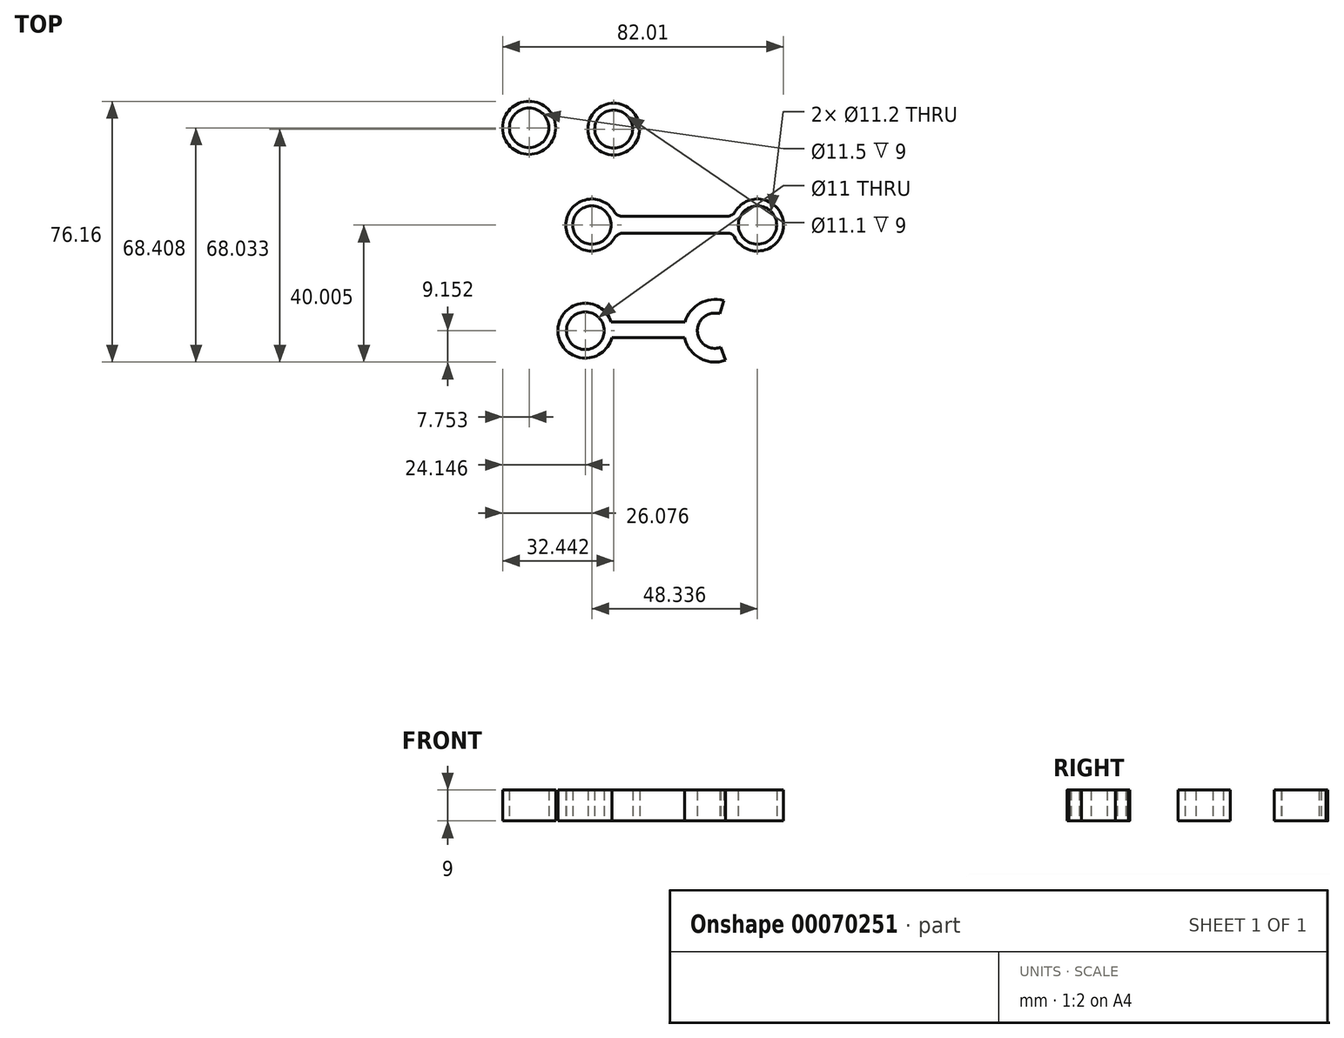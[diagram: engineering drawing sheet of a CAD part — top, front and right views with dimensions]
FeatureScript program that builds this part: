
annotation { "Feature Type Name" : "Feature", "Feature Type Description" : "" }
export const myFeature = defineFeature(function(context is Context, id is Id, definition is map)
    precondition{}
    {
        {
            var Q0;
            Q0=qCreatedBy(makeId("Top.planeOp"),FACE);
            var sketch = newSketch(context, id + "F0", { "sketchPlane" : qUnion([Q0])});
            skCircle(sketch, "E0", {"center": v(-32.87, 26.06) * mm, "radius": 5.6 * mm});
            skCircle(sketch, "E1", {"center": v(15.46, 26.06) * mm, "radius": 5.6 * mm});
            skCircle(sketch, "E2", {"center": v(-34.8, -4.8) * mm, "radius": 5.5 * mm});
            skCircle(sketch, "E3", {"center": v(3.08, -4.8) * mm, "radius": 5.15 * mm});
            skLineSegment(sketch, "E4", {"start": v(-32.87, 26.06) * mm, "end": v(15.46, 26.06) * mm});
            skLineSegment(sketch, "E5", {"start": v(3.08, -4.8) * mm, "end": v(-34.8, -4.8) * mm});
            skCircle(sketch, "E6", {"center": v(-32.87, 26.06) * mm, "radius": 7.6 * mm});
            skCircle(sketch, "E7", {"center": v(15.46, 26.06) * mm, "radius": 7.6 * mm});
            skCircle(sketch, "E8", {"center": v(-34.8, -4.8) * mm, "radius": 8 * mm});
            skCircle(sketch, "E9", {"center": v(3.08, -4.8) * mm, "radius": 9.15 * mm});
            skLineSegment(sketch, "E10", {"start": v(15.46, 26.06) * mm, "end": v(20.01, 32.14) * mm});
            skLineSegment(sketch, "E11", {"start": v(15.46, 26.06) * mm, "end": v(13.27, 18.78) * mm});
            skLineSegment(sketch, "E12", {"start": v(3.08, -4.8) * mm, "end": v(5.57, 4) * mm});
            skLineSegment(sketch, "E13", {"start": v(3.08, -4.8) * mm, "end": v(6.09, -13.44) * mm});
            skLineSegment(sketch, "E14", {"start": v(-25.72, 28.6) * mm, "end": v(8.3, 28.6) * mm});
            skLineSegment(sketch, "E15", {"start": v(-25.66, 23.67) * mm, "end": v(8.25, 23.67) * mm});
            skLineSegment(sketch, "E16", {"start": v(-27.22, -2.25) * mm, "end": v(-5.71, -2.25) * mm});
            skLineSegment(sketch, "E17", {"start": v(-27.08, -6.86) * mm, "end": v(-5.84, -6.86) * mm});
            skCircle(sketch, "E18", {"center": v(-23.97, 31.37) * mm, "radius": 2.77 * mm});
            skCircle(sketch, "E19", {"center": v(-23.82, 20.8) * mm, "radius": 2.87 * mm});
            skCircle(sketch, "E20", {"center": v(6.54, 31.42) * mm, "radius": 2.81 * mm});
            skCircle(sketch, "E21", {"center": v(7, 21.78) * mm, "radius": 1.89 * mm});
            skSolve(sketch);
        }
        {
            var Q0;
            Q0=makeQuery(id+"F0.imprint","IMPRINT",FACE,{"disambiguationData":[TD([[makeQuery(id+"F0.imprint","IMPRINT",EDGE,{"derivedFrom":sQuery(id+"F0.wireOp",EDGE,"E0")}),-1.0]])]});
            var Q1;
            {var subQ5=sQuery(id+"F0.wireOp",EDGE,"E15");Q1=makeQuery(id+"F0.imprint","IMPRINT",FACE,{"disambiguationData":[TD([[makeQuery(id+"F0.imprint","IMPRINT",EDGE,{"derivedFrom":subQ5}),1.0]])]});}
            var Q2;
            {var subQ5=sQuery(id+"F0.wireOp",EDGE,"E14");Q2=makeQuery(id+"F0.imprint","IMPRINT",FACE,{"disambiguationData":[TD([[makeQuery(id+"F0.imprint","IMPRINT",EDGE,{"derivedFrom":subQ5}),-1.0]])]});}
            var Q3;
            {var subQ4=sQuery(id+"F0.wireOp",EDGE,"E4");var subQ6=sQuery(id+"F0.wireOp",EDGE,"E1");var subQ7=makeQuery(id+"F0.imprint","INTERSECT",VERTEX,{"derivedFrom":[subQ6,subQ4]});Q3=makeQuery(id+"F0.imprint","IMPRINT",FACE,{"disambiguationData":[TD([[makeQuery(id+"F0.imprint","IMPRINT",EDGE,{"disambiguationData":[TD([[subQ7,-1.0]])],"derivedFrom":subQ6}),-1.0]])]});}
            var Q4;
            {var subQ0=sQuery(id+"F0.wireOp",EDGE,"E4");var subQ1=sQuery(id+"F0.wireOp",EDGE,"E1");var subQ2=makeQuery(id+"F0.imprint","INTERSECT",VERTEX,{"derivedFrom":[subQ1,subQ0]});Q4=makeQuery(id+"F0.imprint","IMPRINT",FACE,{"disambiguationData":[TD([[makeQuery(id+"F0.imprint","IMPRINT",EDGE,{"disambiguationData":[TD([[subQ2,1.0]])],"derivedFrom":subQ1}),-1.0]])]});}
            var Q5;
            Q5=makeQuery(id+"F0.imprint","IMPRINT",FACE,{"disambiguationData":[TD([[makeQuery(id+"F0.imprint","IMPRINT",EDGE,{"derivedFrom":sQuery(id+"F0.wireOp",EDGE,"E2")}),-1.0]])]});
            var Q6;
            {var subQ5=sQuery(id+"F0.wireOp",EDGE,"E16");Q6=makeQuery(id+"F0.imprint","IMPRINT",FACE,{"disambiguationData":[TD([[makeQuery(id+"F0.imprint","IMPRINT",EDGE,{"derivedFrom":subQ5}),-1.0]])]});}
            var Q7;
            {var subQ5=sQuery(id+"F0.wireOp",EDGE,"E17");Q7=makeQuery(id+"F0.imprint","IMPRINT",FACE,{"disambiguationData":[TD([[makeQuery(id+"F0.imprint","IMPRINT",EDGE,{"derivedFrom":subQ5}),1.0]])]});}
            var Q8;
            {var subQ4=sQuery(id+"F0.wireOp",EDGE,"E5");var subQ6=sQuery(id+"F0.wireOp",EDGE,"E3");var subQ7=makeQuery(id+"F0.imprint","INTERSECT",VERTEX,{"derivedFrom":[subQ6,subQ4]});Q8=makeQuery(id+"F0.imprint","IMPRINT",FACE,{"disambiguationData":[TD([[makeQuery(id+"F0.imprint","IMPRINT",EDGE,{"disambiguationData":[TD([[subQ7,-1.0]])],"derivedFrom":subQ6}),-1.0]])]});}
            var Q9;
            {var subQ2=sQuery(id+"F0.wireOp",EDGE,"E5");var subQ6=sQuery(id+"F0.wireOp",EDGE,"E3");var subQ7=makeQuery(id+"F0.imprint","INTERSECT",VERTEX,{"derivedFrom":[subQ6,subQ2]});Q9=makeQuery(id+"F0.imprint","IMPRINT",FACE,{"disambiguationData":[TD([[makeQuery(id+"F0.imprint","IMPRINT",EDGE,{"disambiguationData":[TD([[subQ7,1.0]])],"derivedFrom":subQ6}),-1.0]])]});}
            var Q10;
            {var subQ0=sQuery(id+"F0.wireOp",EDGE,"E10");var subQ1=sQuery(id+"F0.wireOp",EDGE,"E1");var subQ2=makeQuery(id+"F0.imprint","INTERSECT",VERTEX,{"derivedFrom":[subQ1,subQ0]});Q10=makeQuery(id+"F0.imprint","IMPRINT",FACE,{"disambiguationData":[TD([[makeQuery(id+"F0.imprint","IMPRINT",EDGE,{"disambiguationData":[TD([[subQ2,1.0]])],"derivedFrom":subQ1}),-1.0]])]});}
            var Q11;
            {var subQ0=sQuery(id+"F0.wireOp",EDGE,"E14");var subQ1=sQuery(id+"F0.wireOp",EDGE,"E6");var subQ2=makeQuery(id+"F0.imprint","INTERSECT",VERTEX,{"derivedFrom":[subQ1,subQ0]});Q11=makeQuery(id+"F0.imprint","IMPRINT",FACE,{"disambiguationData":[TD([[makeQuery(id+"F0.imprint","IMPRINT",EDGE,{"disambiguationData":[TD([[subQ2,-1.0]])],"derivedFrom":subQ1}),-1.0]])]});}
            var Q12;
            {var subQ0=sQuery(id+"F0.wireOp",EDGE,"E15");var subQ1=sQuery(id+"F0.wireOp",EDGE,"E6");var subQ2=makeQuery(id+"F0.imprint","INTERSECT",VERTEX,{"derivedFrom":[subQ1,subQ0]});Q12=makeQuery(id+"F0.imprint","IMPRINT",FACE,{"disambiguationData":[TD([[makeQuery(id+"F0.imprint","IMPRINT",EDGE,{"disambiguationData":[TD([[subQ2,1.0]])],"derivedFrom":subQ1}),-1.0]])]});}
            var Q13;
            {var subQ0=sQuery(id+"F0.wireOp",EDGE,"E14");var subQ1=sQuery(id+"F0.wireOp",EDGE,"E7");var subQ2=makeQuery(id+"F0.imprint","INTERSECT",VERTEX,{"derivedFrom":[subQ1,subQ0]});Q13=makeQuery(id+"F0.imprint","IMPRINT",FACE,{"disambiguationData":[TD([[makeQuery(id+"F0.imprint","IMPRINT",EDGE,{"disambiguationData":[TD([[subQ2,1.0]])],"derivedFrom":subQ1}),-1.0]])]});}
            var Q14;
            {var subQ0=sQuery(id+"F0.wireOp",EDGE,"E15");var subQ1=sQuery(id+"F0.wireOp",EDGE,"E7");var subQ2=makeQuery(id+"F0.imprint","INTERSECT",VERTEX,{"derivedFrom":[subQ1,subQ0]});Q14=makeQuery(id+"F0.imprint","IMPRINT",FACE,{"disambiguationData":[TD([[makeQuery(id+"F0.imprint","IMPRINT",EDGE,{"disambiguationData":[TD([[subQ2,-1.0]])],"derivedFrom":subQ1}),-1.0]])]});}
            extrude(context, id + "F1", {"entities" : qUnion([Q0, Q1, Q2, Q3, Q4, Q5, Q6, Q7, Q8, Q9, Q10, Q11, Q12, Q13, Q14]), "depth" : 9 * mm});
        }
        {
            var Q0;
            Q0=qCreatedBy(makeId("Top.planeOp"),FACE);
            var sketch = newSketch(context, id + "F2", { "sketchPlane" : qUnion([Q0])});
            skCircle(sketch, "E22", {"center": v(-51.2, 54.46) * mm, "radius": 5.75 * mm});
            skCircle(sketch, "E23", {"center": v(-51.2, 54.46) * mm, "radius": 7.75 * mm});
            skCircle(sketch, "E24", {"center": v(-26.5, 54.08) * mm, "radius": 5.55 * mm});
            skCircle(sketch, "E25", {"center": v(-26.5, 54.08) * mm, "radius": 7.55 * mm});
            skSolve(sketch);
        }
        {
            var Q0;
            Q0=makeQuery(id+"F2.imprint","IMPRINT",FACE,{"disambiguationData":[TD([[makeQuery(id+"F2.imprint","IMPRINT",EDGE,{"derivedFrom":sQuery(id+"F2.wireOp",EDGE,"E22")}),-1.0]])]});
            var Q1;
            Q1=makeQuery(id+"F2.imprint","IMPRINT",FACE,{"disambiguationData":[TD([[makeQuery(id+"F2.imprint","IMPRINT",EDGE,{"derivedFrom":sQuery(id+"F2.wireOp",EDGE,"E24")}),-1.0]])]});
            extrude(context, id + "F3", {"entities" : qUnion([Q0, Q1]), "depth" : 9 * mm});
        }
    });
